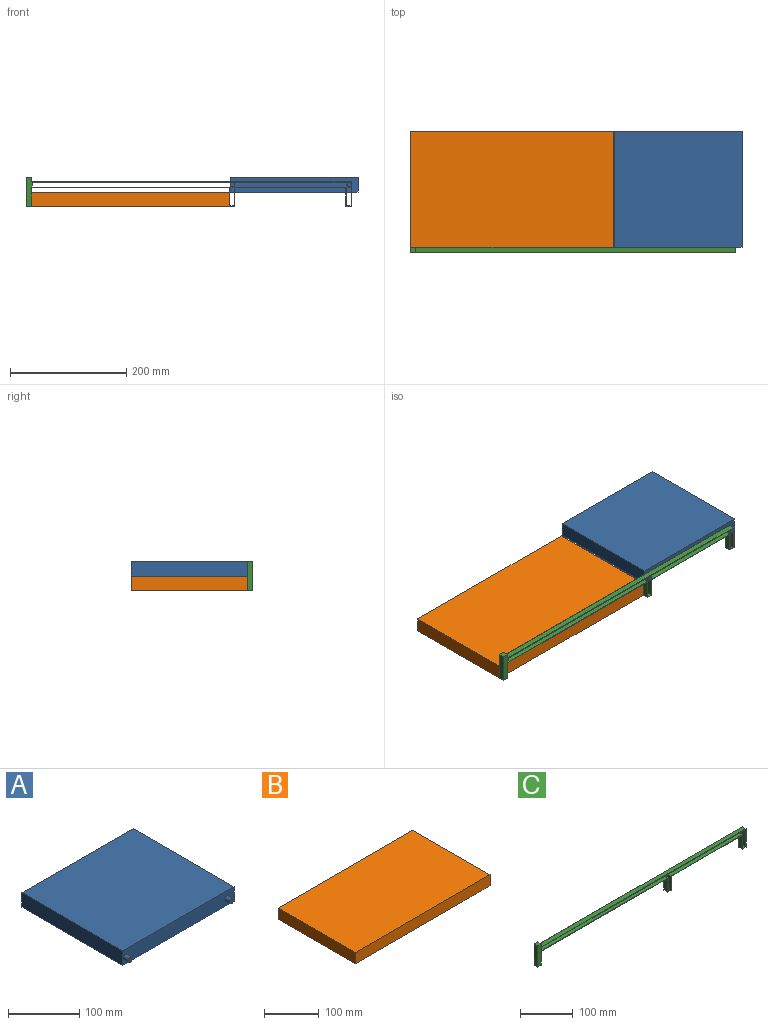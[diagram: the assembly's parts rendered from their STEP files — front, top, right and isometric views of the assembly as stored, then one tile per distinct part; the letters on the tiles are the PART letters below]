
ASSEMBLY  parts=3 mates=1
PART A: 10 faces, bbox 220x210x25 mm
  f0: plane 200x25mm, normal (-1,0,0), area 5000mm2, adj f1,f3,f4,f5
  f1: plane 220x25mm, normal (0,-1,0), area 5399.5mm2, adj f0,f2,f4,f5,f6,f8
  f2: plane 200x25mm, normal (1,0,0), area 5000mm2, adj f1,f3,f4,f5
  f3: plane 220x25mm, normal (0,1,0), area 5500mm2, adj f0,f2,f4,f5
  f4: plane 220x200mm, normal (0,0,1), area 44000mm2, adj f0,f1,f2,f3
  f5: plane 220x200mm, normal (0,0,-1), area 44000mm2, adj f0,f1,f2,f3
  f6: cylinder r=4mm len=10mm, axis (0,1,0), area 251.3mm2, adj f1,f7
  f7: plane 8x8mm, normal (0,-1,0), area 50.3mm2, adj f6
  f8: cylinder r=4mm len=10mm, axis (0,1,0), area 251.3mm2, adj f1,f9
  f9: plane 8x8mm, normal (0,-1,0), area 50.3mm2, adj f8
PART B: 6 faces, bbox 350x200x25 mm
  f0: plane 350x25mm, normal (0,1,0), area 8750mm2, adj f1,f3,f4,f5
  f1: plane 200x25mm, normal (-1,0,0), area 5000mm2, adj f0,f2,f4,f5
  f2: plane 350x25mm, normal (0,-1,0), area 8750mm2, adj f1,f3,f4,f5
  f3: plane 200x25mm, normal (1,0,0), area 5000mm2, adj f0,f2,f4,f5
  f4: plane 350x200mm, normal (0,0,1), area 70000mm2, adj f0,f1,f2,f3
  f5: plane 350x200mm, normal (0,0,-1), area 70000mm2, adj f0,f1,f2,f3
PART C: 26 faces, bbox 561x10x50 mm
  f0: plane 32.5x10mm, normal (1,0,0), area 325mm2, adj f1,f23,f24,f25
  f1: plane 340x10mm, normal (0,0,1), area 3400mm2, adj f0,f2,f24,f25
  f2: plane 10x8mm, normal (1,0,0), area 80mm2, adj f1,f3,f24,f25
  f3: plane 549x10mm, normal (0,0,-1), area 5490mm2, adj f2,f4,f24,f25
  f4: plane 40.5x10mm, normal (-1,0,0), area 405mm2, adj f3,f5,f24,f25
  f5: plane 10x8mm, normal (0,0,1), area 80mm2, adj f4,f6,f24,f25
  f6: plane 32.5x10mm, normal (1,0,0), area 325mm2, adj f5,f7,f24,f25
  f7: plane 193x10mm, normal (0,0,1), area 1930mm2, adj f6,f8,f24,f25
  f8: plane 32.5x10mm, normal (-1,0,0), area 325mm2, adj f7,f23,f24,f25
  f9: plane 340x10mm, normal (0,0,-1), area 3400mm2, adj f10,f22,f24,f25
  f10: plane 32.5x10mm, normal (-1,0,0), area 325mm2, adj f9,f11,f24,f25
  f11: plane 10x10mm, normal (0,0,-1), area 100mm2, adj f10,f12,f24,f25
  f12: plane 32.5x10mm, normal (1,0,0), area 325mm2, adj f11,f13,f24,f25
  f13: plane 191x10mm, normal (0,0,-1), area 1910mm2, adj f12,f14,f24,f25
  f14: plane 32.5x10mm, normal (-1,0,0), area 325mm2, adj f13,f15,f24,f25
  f15: plane 10x10mm, normal (0,0,-1), area 100mm2, adj f14,f16,f24,f25
  f16: plane 42.5x10mm, normal (1,0,0), area 425mm2, adj f15,f17,f24,f25
  f17: plane 551x10mm, normal (0,0,1), area 5510mm2, adj f16,f18,f24,f25
  f18: plane 10x7.5mm, normal (1,0,0), area 75mm2, adj f17,f19,f24,f25
  f19: plane 10x10mm, normal (0,0,1), area 100mm2, adj f18,f20,f24,f25
  f20: plane 50x10mm, normal (-1,0,0), area 500mm2, adj f19,f21,f24,f25
  f21: plane 10x10mm, normal (0,0,-1), area 100mm2, adj f20,f22,f24,f25
  f22: plane 32.5x10mm, normal (1,0,0), area 325mm2, adj f9,f21,f24,f25
  f23: plane 10x8mm, normal (0,0,1), area 80mm2, adj f0,f8,f24,f25
  f24: plane 561x50mm, normal (0,-1,0), area 1748mm2, adj f0,f1,f2,f3,f4,f5,f6,f7
  f25: plane 561x50mm, normal (0,1,0), area 1748mm2, adj f0,f1,f2,f3,f4,f5,f6,f7
PLACE A t=(287,0,25)mm
PLACE B at identity fixed
PLACE C at identity
MATE fastened C.f25 <-> B.f2  axis (0,1,0) through (-175,-100,0)mm
